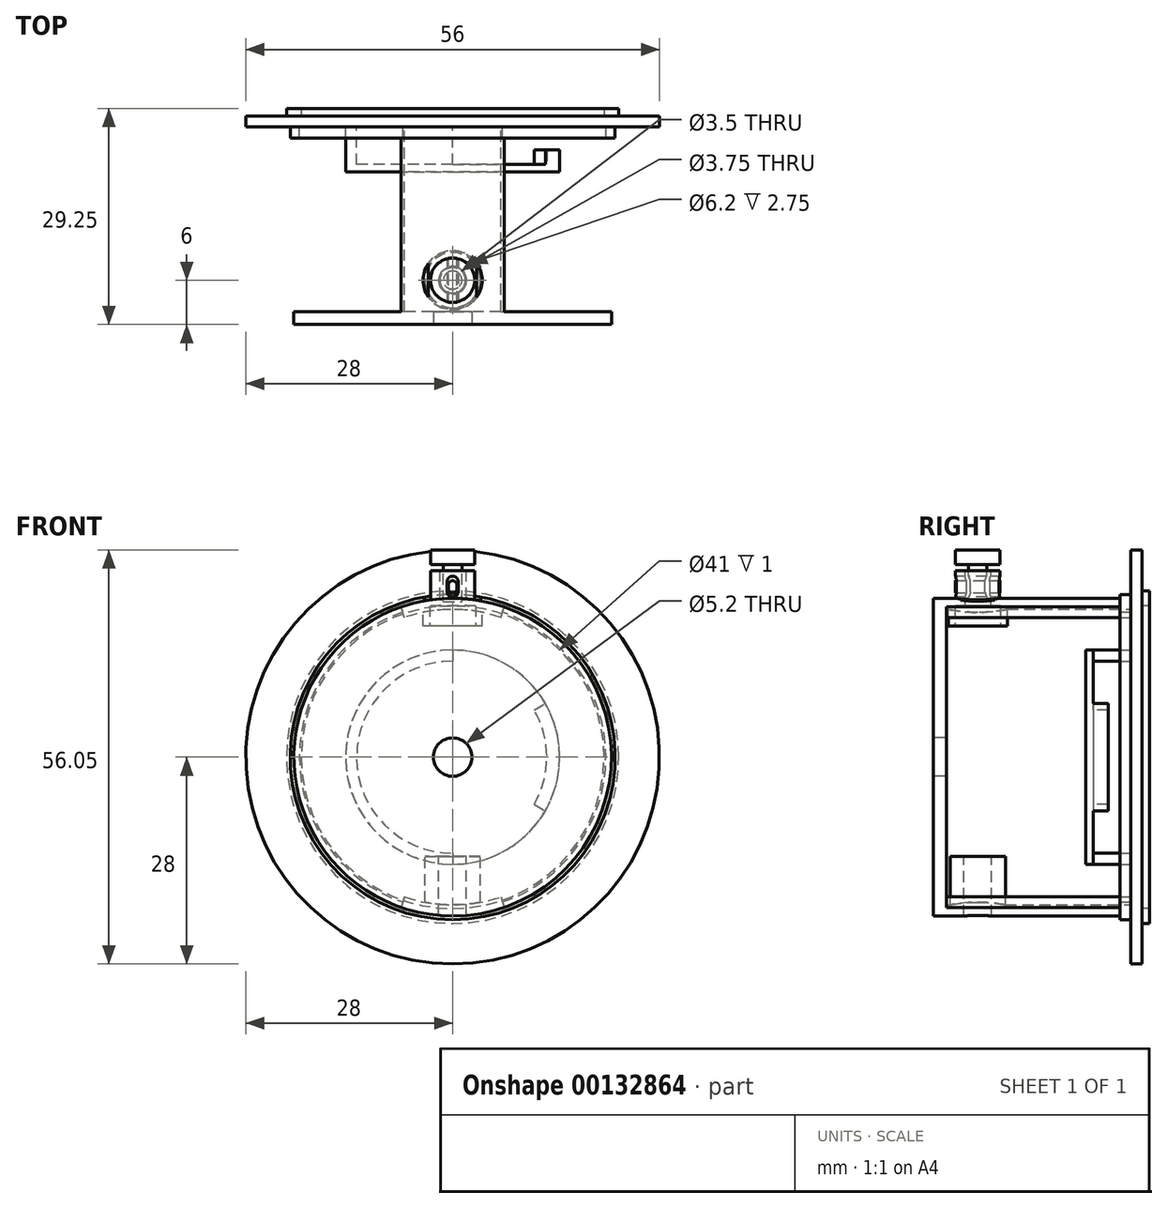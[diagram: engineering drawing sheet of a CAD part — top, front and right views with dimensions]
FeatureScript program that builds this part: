
annotation { "Feature Type Name" : "Feature", "Feature Type Description" : "" }
export const myFeature = defineFeature(function(context is Context, id is Id, definition is map)
    precondition{}
    {
        {
            var Q0;
            Q0=qCreatedBy(makeId("Front.planeOp"),FACE);
            var sketch = newSketch(context, id + "F0", { "sketchPlane" : qUnion([Q0])});
            skCircle(sketch, "E0", {"center": v(0, 0) * mm, "radius": 28 * mm});
            skSolve(sketch);
        }
        {
            var Q0;
            Q0=qSketchRegion(id+"F0",true);
            extrude(context, id + "F1", {"entities" : qUnion([Q0]), "depth" : 1.5 * mm});
        }
        {
            var Q0;
            Q0=makeQuery(id+"F1.opExtrude","CAP_FACE",FACE,{"disambiguationData":[OSD([sQuery(id+"F0.wireOp",EDGE,"E0")])],"isStart":false});
            var sketch = newSketch(context, id + "F2", { "sketchPlane" : qUnion([Q0])});
            skArc(sketch, "E1", {"start": v(0, 13) * mm, "mid": v(-13, 0) * mm, "end": v(0, -13) * mm});
            skArc(sketch, "E2", {"start": v(0, 14.5) * mm, "mid": v(-14.5, 0) * mm, "end": v(0, -14.5) * mm});
            skLineSegment(sketch, "E3", {"start": v(0, 14.5) * mm, "end": v(0, 13) * mm});
            skLineSegment(sketch, "E4.trimOffspring", {"start": v(0, -13) * mm, "end": v(0, -14.5) * mm});
            skSolve(sketch);
        }
        {
            var Q0;
            Q0=qSketchRegion(id+"F2",true);
            extrude(context, id + "F3", {"entities" : qUnion([Q0]), "operationType" : NewBodyOperationType.ADD, "depth" : 5.1 * mm});
        }
        {
            var Q0;
            {var subQ0=sQuery(id+"F0.wireOp",EDGE,"E0");Q0=makeQuery(id+"F3.boolean.opBoolean","SPLIT",FACE,{"disambiguationData":[TD([makeQuery(id+"F1.opExtrude","SWEPT_FACE",FACE,{"disambiguationData":[OSD([subQ0])]})])],"derivedFrom":makeQuery(id+"F1.opExtrude","CAP_FACE",FACE,{"disambiguationData":[OSD([subQ0])],"isStart":false})});}
            var sketch = newSketch(context, id + "F4", { "sketchPlane" : qUnion([Q0])});
            skArc(sketch, "E5", {"start": v(7, 20.33) * mm, "mid": v(0, 21.5) * mm, "end": v(-7, 20.33) * mm});
            skArc(sketch, "E6", {"start": v(6.51, 18.91) * mm, "mid": v(0, 20) * mm, "end": v(-6.51, 18.91) * mm});
            skLineSegment(sketch, "E7", {"start": v(0, 30.17) * mm, "end": v(0, -31.06) * mm, "construction": true});
            skLineSegment(sketch, "E8", {"start": v(-6.51, 18.91) * mm, "end": v(-7, 20.33) * mm});
            skLineSegment(sketch, "E9", {"start": v(6.51, 18.91) * mm, "end": v(7, 20.33) * mm});
            skArc(sketch, "E10.1.0", {"start": v(-6.51, -18.91) * mm, "mid": v(0, -20) * mm, "end": v(6.51, -18.91) * mm});
            skArc(sketch, "E10.1.1", {"start": v(-7, -20.33) * mm, "mid": v(0, -21.5) * mm, "end": v(7, -20.33) * mm});
            skLineSegment(sketch, "E10.1.2", {"start": v(-6.51, -18.91) * mm, "end": v(-7, -20.33) * mm});
            skLineSegment(sketch, "E10.1.3", {"start": v(6.51, -18.91) * mm, "end": v(7, -20.33) * mm});
            skSolve(sketch);
        }
        {
            var Q0;
            Q0=qSketchRegion(id+"F4",true);
            extrude(context, id + "F5", {"entities" : qUnion([Q0]), "operationType" : NewBodyOperationType.ADD, "depth" : 25 * mm});
        }
        {
            var Q0;
            Q0=makeQuery(id+"F5.opExtrude","CAP_FACE",FACE,{"disambiguationData":[OSD([sQuery(id+"F4.wireOp",EDGE,"E10.1.0"),sQuery(id+"F4.wireOp",EDGE,"E10.1.1"),sQuery(id+"F4.wireOp",EDGE,"E10.1.2"),sQuery(id+"F4.wireOp",EDGE,"E10.1.3")])],"isStart":false});
            var sketch = newSketch(context, id + "F6", { "sketchPlane" : qUnion([Q0])});
            skCircle(sketch, "E11", {"center": v(0, 0) * mm, "radius": 21.5 * mm});
            skSolve(sketch);
        }
        {
            var Q0;
            Q0=qSketchRegion(id+"F6",true);
            extrude(context, id + "F7", {"entities" : qUnion([Q0]), "operationType" : NewBodyOperationType.ADD, "depth" : 1.75 * mm});
        }
        {
            var Q0;
            Q0=makeQuery(id+"F7.opExtrude","CAP_FACE",FACE,{"disambiguationData":[OSD([sQuery(id+"F6.wireOp",EDGE,"E11")])],"isStart":false});
            var sketch = newSketch(context, id + "F8", { "sketchPlane" : qUnion([Q0])});
            skCircle(sketch, "E12", {"center": v(0, 0) * mm, "radius": 2.6 * mm});
            skSolve(sketch);
        }
        {
            var Q0;
            Q0=qSketchRegion(id+"F8",true);
            extrude(context, id + "F9", {"entities" : qUnion([Q0]), "operationType" : NewBodyOperationType.REMOVE, "oppositeDirection" : true, "depth" : 25 * mm});
        }
        {
            var Q0;
            Q0=qCreatedBy(makeId("Top.planeOp"),FACE);
            var sketch = newSketch(context, id + "F10", { "sketchPlane" : qUnion([Q0])});
            skCircle(sketch, "E13", {"center": v(0, -22.25) * mm, "radius": 1.98 * mm});
            skSolve(sketch);
        }
        {
            var Q0;
            Q0=qSketchRegion(id+"F10",true);
            extrude(context, id + "F11", {"entities" : qUnion([Q0]), "operationType" : NewBodyOperationType.REMOVE, "oppositeDirection" : true, "depth" : 30 * mm});
        }
        {
            var Q0;
            Q0=qCreatedBy(makeId("Top.planeOp"),FACE);
            var sketch = newSketch(context, id + "F12", { "sketchPlane" : qUnion([Q0])});
            skCircle(sketch, "E14", {"center": v(0, -22.25) * mm, "radius": 1.88 * mm});
            skCircle(sketch, "E15", {"center": v(0, -22.25) * mm, "radius": 3.75 * mm});
            skSolve(sketch);
        }
        {
            var Q0;
            Q0=makeQuery(id+"F12.imprint","IMPRINT",FACE,{"disambiguationData":[TD([[makeQuery(id+"F12.imprint","IMPRINT",EDGE,{"derivedFrom":sQuery(id+"F12.wireOp",EDGE,"E14")}),-1.0]])]});
            var Q1;
            Q1=makeQuery(id+"F5.opExtrude","SWEPT_FACE",FACE,{"disambiguationData":[OSD([sQuery(id+"F4.wireOp",EDGE,"E10.1.1")])]});
            var Q2;
            Q2=makeQuery(id+"F1.opExtrude","SWEPT_BODY",BODY,{"disambiguationData":[OSD([sQuery(id+"F0.wireOp",EDGE,"E0")])]});
            var Q3;
            Q3=makeQuery(id+"F5.opExtrude","SWEPT_FACE",FACE,{"disambiguationData":[OSD([sQuery(id+"F4.wireOp",EDGE,"E6")])]});
            var Q4;
            Q4=makeQuery(id+"F1.opExtrude","SWEPT_BODY",BODY,{"disambiguationData":[OSD([sQuery(id+"F0.wireOp",EDGE,"E0")])]});
            extrude(context, id + "F13", {"entities" : qUnion([Q0]), "operationType" : NewBodyOperationType.ADD, "endBound" : BoundingType.UP_TO_SURFACE, "oppositeDirection" : true, "endBoundEntityFace" : qUnion([Q1]), "endBoundEntityBody" : qUnion([Q2]), "depth" : 25 * mm, "offsetDistance" : 25 * mm});
        }
        {
            var Q0;
            Q0=qCreatedBy(makeId("Right.planeOp"),FACE);
            var sketch = newSketch(context, id + "F14", { "sketchPlane" : qUnion([Q0])});
            skLineSegment(sketch, "E16.bottom", {"start": v(-10.25, 13.41) * mm, "end": v(-26.25, 13.41) * mm});
            skLineSegment(sketch, "E16.top", {"start": v(-10.25, -13.41) * mm, "end": v(-26.25, -13.41) * mm});
            skLineSegment(sketch, "E16.left", {"start": v(-10.25, 13.41) * mm, "end": v(-10.25, -13.41) * mm});
            skLineSegment(sketch, "E16.right", {"start": v(-26.25, 13.41) * mm, "end": v(-26.25, -13.41) * mm});
            skSolve(sketch);
        }
        {
            var Q0;
            Q0=qSketchRegion(id+"F14",true);
            extrude(context, id + "F15", {"entities" : qUnion([Q0]), "operationType" : NewBodyOperationType.REMOVE, "oppositeDirection" : true, "depth" : 25 * mm, "hasSecondDirection" : true, "secondDirectionOppositeDirection" : false, "secondDirectionDepth" : 25 * mm});
        }
        {
            var Q0;
            Q0=makeQuery(id+"F3.opExtrude","CAP_FACE",FACE,{"disambiguationData":[OSD([sQuery(id+"F2.wireOp",EDGE,"E1"),sQuery(id+"F2.wireOp",EDGE,"E2"),sQuery(id+"F2.wireOp",EDGE,"E3"),sQuery(id+"F2.wireOp",EDGE,"E4.trimOffspring")])],"isStart":false});
            var sketch = newSketch(context, id + "F16", { "sketchPlane" : qUnion([Q0])});
            skCircle(sketch, "E17", {"center": v(0, 0) * mm, "radius": 14.5 * mm});
            skSolve(sketch);
        }
        {
            var Q0;
            Q0=qSketchRegion(id+"F16",true);
            extrude(context, id + "F17", {"entities" : qUnion([Q0]), "operationType" : NewBodyOperationType.ADD, "depth" : 1 * mm});
        }
        {
            var Q0;
            Q0=makeQuery(id+"F17.opExtrude","CAP_FACE",FACE,{"disambiguationData":[OSD([sQuery(id+"F16.wireOp",EDGE,"E17")])],"isStart":true});
            var sketch = newSketch(context, id + "F18", { "sketchPlane" : qUnion([Q0])});
            skArc(sketch, "E18", {"start": v(-12.56, 7.25) * mm, "mid": v(-14.5, 0) * mm, "end": v(-12.56, -7.25) * mm});
            skArc(sketch, "E19", {"start": v(-11.04, 6.37) * mm, "mid": v(-12.75, 0) * mm, "end": v(-11.04, -6.38) * mm});
            skLineSegment(sketch, "E20", {"start": v(0, 14.5) * mm, "end": v(0, -14.5) * mm, "construction": true});
            skLineSegment(sketch, "E21", {"start": v(-11.04, 6.38) * mm, "end": v(-12.56, 7.25) * mm});
            skLineSegment(sketch, "E22", {"start": v(-11.04, -6.38) * mm, "end": v(-12.56, -7.25) * mm});
            skSolve(sketch);
        }
        {
            var Q0;
            Q0=qSketchRegion(id+"F18",true);
            extrude(context, id + "F19", {"entities" : qUnion([Q0]), "operationType" : NewBodyOperationType.ADD, "depth" : 2 * mm});
        }
        {
            var Q0;
            Q0=qCreatedBy(makeId("Top.planeOp"),FACE);
            cPlane(context, id + "F20", {"entities" : qUnion([Q0]), "cplaneType" : CPlaneType.OFFSET, "offset" : 15 * mm, "width" : 150 * mm, "height" : 150 * mm});
        }
        {
            var Q0;
            Q0=makeQuery(id+"F1.opExtrude","CAP_FACE",FACE,{"disambiguationData":[OSD([sQuery(id+"F0.wireOp",EDGE,"E0")])],"isStart":true});
            var sketch = newSketch(context, id + "F21", { "sketchPlane" : qUnion([Q0])});
            skCircle(sketch, "E23", {"center": v(0, 0) * mm, "radius": 22.5 * mm});
            skCircle(sketch, "E24", {"center": v(0, 0) * mm, "radius": 20.5 * mm});
            skSolve(sketch);
        }
        {
            var Q0;
            Q0=qSketchRegion(id+"F21",true);
            extrude(context, id + "F22", {"entities" : qUnion([Q0]), "operationType" : NewBodyOperationType.ADD, "depth" : 1 * mm});
        }
        {
            var Q0;
            Q0=makeQuery(id+"F1.opExtrude","CAP_FACE",FACE,{"disambiguationData":[OSD([sQuery(id+"F0.wireOp",EDGE,"E0")])],"isStart":false});
            var sketch = newSketch(context, id + "F23", { "sketchPlane" : qUnion([Q0])});
            skCircle(sketch, "E25", {"center": v(0, 0) * mm, "radius": 22 * mm});
            skCircle(sketch, "E26", {"center": v(0, 0) * mm, "radius": 20.75 * mm});
            skSolve(sketch);
        }
        {
            var Q0;
            Q0=qSketchRegion(id+"F23",true);
            extrude(context, id + "F24", {"entities" : qUnion([Q0]), "operationType" : NewBodyOperationType.ADD, "depth" : 1.5 * mm});
        }
        {
            var Q0;
            Q0=qCreatedBy(id+"F20.planeOp",FACE);
            var sketch = newSketch(context, id + "F25", { "sketchPlane" : qUnion([Q0])});
            skCircle(sketch, "E27", {"center": v(0, -22.25) * mm, "radius": 3.1 * mm});
            skSolve(sketch);
        }
        {
            var Q0;
            Q0=qSketchRegion(id+"F25",true);
            extrude(context, id + "F26", {"entities" : qUnion([Q0]), "operationType" : NewBodyOperationType.REMOVE, "depth" : 5.5 * mm});
        }
        {
            var Q0;
            Q0=qCreatedBy(id+"F20.planeOp",FACE);
            cPlane(context, id + "F27", {"entities" : qUnion([Q0]), "cplaneType" : CPlaneType.OFFSET, "offset" : 6.25 * mm, "width" : 150 * mm, "height" : 150 * mm});
        }
        {
            var Q0;
            Q0=qCreatedBy(id+"F27.planeOp",FACE);
            var sketch = newSketch(context, id + "F28", { "sketchPlane" : qUnion([Q0])});
            skCircle(sketch, "E28", {"center": v(0, -22.25) * mm, "radius": 3 * mm});
            skCircle(sketch, "E29", {"center": v(0, -22.25) * mm, "radius": 1.75 * mm});
            skSolve(sketch);
        }
        {
            var Q0;
            Q0=qSketchRegion(id+"F28",true);
            extrude(context, id + "F29", {"entities" : qUnion([Q0]), "operationType" : NewBodyOperationType.ADD, "depth" : 4 * mm});
        }
        {
            var Q0;
            Q0=makeQuery(id+"F26.boolean.opBoolean","COPY",FACE,{"derivedFrom":makeQuery(id+"F26.opExtrude","CAP_FACE",FACE,{"disambiguationData":[OSD([sQuery(id+"F25.wireOp",EDGE,"E27")])],"isStart":false})});
            var sketch = newSketch(context, id + "F30", { "sketchPlane" : qUnion([Q0])});
            skCircle(sketch, "E30", {"center": v(0, 22.25) * mm, "radius": 1.75 * mm});
            skSolve(sketch);
        }
        {
            var Q0;
            Q0=qSketchRegion(id+"F30",true);
            extrude(context, id + "F31", {"entities" : qUnion([Q0]), "operationType" : NewBodyOperationType.REMOVE, "oppositeDirection" : true, "depth" : 25 * mm});
        }
        {
            var Q0;
            Q0=qCreatedBy(id+"F27.planeOp",FACE);
            var sketch = newSketch(context, id + "F32", { "sketchPlane" : qUnion([Q0])});
            skCircle(sketch, "E31", {"center": v(0, -22.25) * mm, "radius": 4 * mm});
            skCircle(sketch, "E32", {"center": v(0, -22.25) * mm, "radius": 3.1 * mm});
            skSolve(sketch);
        }
        {
            var Q0;
            Q0=qSketchRegion(id+"F32",true);
            extrude(context, id + "F33", {"entities" : qUnion([Q0]), "operationType" : NewBodyOperationType.ADD, "oppositeDirection" : true, "depth" : 3.5 * mm});
        }
        {
            var Q0;
            Q0=makeQuery(id+"F7.opExtrude","CAP_FACE",FACE,{"disambiguationData":[OSD([sQuery(id+"F6.wireOp",EDGE,"E11")])],"isStart":false});
            cPlane(context, id + "F34", {"entities" : qUnion([Q0]), "cplaneType" : CPlaneType.OFFSET, "offset" : 6 * mm, "oppositeDirection" : true, "width" : 150 * mm, "height" : 150 * mm});
        }
        {
            var Q0;
            Q0=makeQuery(id+"F29.opExtrude","CAP_FACE",FACE,{"disambiguationData":[OSD([sQuery(id+"F28.wireOp",EDGE,"E28"),sQuery(id+"F28.wireOp",EDGE,"E29")])],"isStart":false});
            cPlane(context, id + "F35", {"entities" : qUnion([Q0]), "cplaneType" : CPlaneType.OFFSET, "offset" : 2.8 * mm, "width" : 150 * mm, "height" : 150 * mm});
        }
        {
            var Q0;
            Q0=qCreatedBy(id+"F35.planeOp",FACE);
            var sketch = newSketch(context, id + "F36", { "sketchPlane" : qUnion([Q0])});
            skCircle(sketch, "E33", {"center": v(0, -22.25) * mm, "radius": 3 * mm});
            skSolve(sketch);
        }
        {
            var Q0;
            Q0=makeQuery(id+"F36.imprint","IMPRINT",FACE,{"disambiguationData":[TD([[makeQuery(id+"F36.imprint","IMPRINT",EDGE,{"derivedFrom":sQuery(id+"F36.wireOp",EDGE,"E33")}),1.0]])]});
            extrude(context, id + "F37", {"entities" : qUnion([Q0]), "operationType" : NewBodyOperationType.ADD, "oppositeDirection" : true, "depth" : 2 * mm});
        }
        {
            var Q0;
            Q0=makeQuery(id+"F37.opExtrude","CAP_FACE",FACE,{"disambiguationData":[OSD([sQuery(id+"F36.wireOp",EDGE,"E33")])],"isStart":false});
            var sketch = newSketch(context, id + "F38", { "sketchPlane" : qUnion([Q0])});
            skCircle(sketch, "E34", {"center": v(0, 22.25) * mm, "radius": 1.25 * mm});
            skSolve(sketch);
        }
        {
            var Q0;
            Q0=qSketchRegion(id+"F38",true);
            extrude(context, id + "F39", {"entities" : qUnion([Q0]), "operationType" : NewBodyOperationType.ADD, "depth" : 5 * mm});
        }
        {
            var Q0;
            {var subQ0=sQuery(id+"F0.wireOp",EDGE,"E0");Q0=makeQuery(id+"F24.boolean.opBoolean","SPLIT",FACE,{"disambiguationData":[TD([makeQuery(id+"F1.opExtrude","SWEPT_FACE",FACE,{"disambiguationData":[OSD([subQ0])]})])],"derivedFrom":makeQuery(id+"F1.opExtrude","CAP_FACE",FACE,{"disambiguationData":[OSD([subQ0])],"isStart":false})});}
            var sketch = newSketch(context, id + "F40", { "sketchPlane" : qUnion([Q0])});
            skCircle(sketch, "E35", {"center": v(0, 0) * mm, "radius": 29 * mm});
            skCircle(sketch, "E36", {"center": v(0, 0) * mm, "radius": 30 * mm});
            skSolve(sketch);
        }
        {
            var Q0;
            Q0=qSketchRegion(id+"F40",true);
            extrude(context, id + "F41", {"entities" : qUnion([Q0]), "operationType" : NewBodyOperationType.REMOVE, "depth" : 25 * mm});
        }
        {
            var Q0;
            Q0=qCreatedBy(id+"F34.planeOp",FACE);
            var sketch = newSketch(context, id + "F42", { "sketchPlane" : qUnion([Q0])});
            skArc(sketch, "E37", {"start": v(0.75, 23.75) * mm, "mid": v(0, 24.5) * mm, "end": v(-0.75, 23.75) * mm});
            skLineSegment(sketch, "E38", {"start": v(-0.75, 23.75) * mm, "end": v(-0.75, 22.4) * mm});
            skLineSegment(sketch, "E39", {"start": v(0.75, 23.75) * mm, "end": v(0.75, 22.4) * mm});
            skArc(sketch, "E40", {"start": v(-0.75, 22.4) * mm, "mid": v(0, 21.65) * mm, "end": v(0.75, 22.4) * mm});
            skPoint(sketch, "E41.orphan", {"position": v(-1.72, 23.75) * mm});
            skSolve(sketch);
        }
        {
            var Q0;
            Q0 = qSketchRegion(id + "F42", true);
            extrude(context, id + "F43", {"entities" : qUnion([Q0]), "operationType" : NewBodyOperationType.REMOVE, "oppositeDirection" : true, "depth" : 5 * mm, "hasSecondDirection" : true, "secondDirectionOppositeDirection" : false, "secondDirectionDepth" : 5 * mm});
        }
        {
            var Q0;
            Q0=qCreatedBy(id+"F34.planeOp",FACE);
            var sketch = newSketch(context, id + "F44", { "sketchPlane" : qUnion([Q0])});
            skArc(sketch, "E42", {"start": v(0.58, 23.3) * mm, "mid": v(0, 23.87) * mm, "end": v(-0.57, 23.3) * mm});
            skArc(sketch, "E43", {"start": v(-0.57, 22.8) * mm, "mid": v(0, 22.22) * mm, "end": v(0.58, 22.8) * mm});
            skLineSegment(sketch, "E44", {"start": v(-0.57, 23.3) * mm, "end": v(-0.57, 22.8) * mm});
            skLineSegment(sketch, "E45", {"start": v(0.58, 23.3) * mm, "end": v(0.58, 22.8) * mm});
            skSolve(sketch);
        }
        {
            var Q0;
            Q0 = qSketchRegion(id + "F44", true);
            extrude(context, id + "F45", {"entities" : qUnion([Q0]), "operationType" : NewBodyOperationType.ADD, "depth" : 3 * mm, "hasSecondDirection" : true, "secondDirectionOppositeDirection" : true, "secondDirectionDepth" : 3 * mm});
        }
    });
